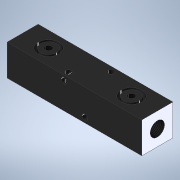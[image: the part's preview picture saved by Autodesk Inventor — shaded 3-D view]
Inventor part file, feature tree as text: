
AUTODESK INVENTOR PART (.ipt)
format: ipt  version: 2021.2 (Build 252289000, 289)  size: 257,024 bytes
history: native  units: in
note: dims shown in document units (in); Inventor stores cm internally (conversion verified against a paired STEP export)
features: sketch x14, hole x11, extrude x3, move_body x2, direct_edit x1
ambient origin geometry x8: Origin, YZ Plane, XZ Plane, XY Plane, X Axis, Y Axis, Z Axis, Center Point
bodies: Solid1 (feature_tree)
feature tree (31):
  extrude  "Extrusion1"  Depth=0.375in
  hole  "Hole3"  [1 undecoded]
  hole  "Hole4"  [1 undecoded]
  hole  "Hole5"  [1 undecoded]
  hole  "Hole6"  [1 undecoded]
  hole  "Hole7"  [1 undecoded]
  extrude  "Extrusion2"  Depth=0.5in
  extrude  "Extrusion3"  Depth=0.5in
  hole  "Hole10"  [1 undecoded]
  hole  "Hole11"  [1 undecoded]
  hole  "Hole12"  [1 undecoded]
  hole  "Hole13"  [1 undecoded]
  direct_edit  "Direct Edit5"
  hole  "Hole14"  [1 undecoded]
  hole  "Hole15"  [1 undecoded]
  sketch  "Sketch1"  dims[d6=0.75in d7=0.0in d34=0.375in]
  sketch  "Sketch4"  dims[d35=0.5in]
  sketch  "Sketch5"  dims[d36=0.156in d37=0.375in d38=0.222in d39=0.25in d40=0.5635in d41=0.375in d42=0.0in d43=0.375in]
  sketch  "Sketch6"  dims[d44=0.156in d45=0.375in d46=0.222in d47=0.25in d48=0.5635in d49=0.375in d50=0.0in d51=1.25in]
  sketch  "Sketch7"  dims[d52=0.116in]
  sketch  "Sketch8"  dims[d53=0.144in d54=0.375in d55=0.119in d56=0.25in d57=0.5635in d58=0.375in d59=0.0in d60=1.25in]
  sketch  "Sketch9"  dims[d61=0.116in]
  sketch  "Sketch11"  dims[d62=0.144in d63=0.375in d64=0.119in d65=0.25in d66=0.5635in d67=0.375in d68=0.0in d69=0.116in]
  sketch  "Sketch13"  dims[d70=1.25in d71=1.25in]
  sketch  "Sketch14"  dims[d72=0.116in]
  sketch  "Sketch15"  dims[d73=0.144in d74=0.375in d75=0.119in d76=0.25in d77=0.5635in d78=0.375in d79=0.0in d82=0.5in]
  sketch  "Sketch16"  dims[d83=0.38in d84=0.5in]
  sketch  "Sketch17"  dims[d85=0.2in d86=0.0in d97=0.38in]
  sketch  "Sketch18"  dims[d98=0.5in d99=0.2in d100=0.0in d113=0.5in d114=0.155in d115=0.0625in d116=0.75in d117=0.119in d118=0.25in d119=0.5635in d120=0.5625in d121=0.0in d122=0.5in d123=0.155in d124=0.0625in d125=0.75in d126=0.119in d127=0.25in d128=0.5635in d129=0.5625in d130=0.0in d131=0.5in d132=0.155in d133=0.156in d134=0.17in d135=0.119in d136=0.25in d137=0.5635in d138=0.17in d139=0.0in d140=0.5in d141=0.155in d142=0.156in d143=0.17in d144=0.119in d145=0.25in d146=0.5635in d147=0.17in d148=0.0in d161=0.125in d162=0.0in d163=0.0in d164=0.0in d165=0.0in d166=0.125in d167=0.375in d168=0.375in d169=0.313in d170=0.2726in d171=0.0246in d172=0.3269in d173=0.375in d174=0.25in d175=0.5635in d176=2.0in d177=0.0in d178=0.375in d179=0.375in d180=0.313in d181=0.2726in d182=0.0246in d183=0.3269in d184=0.375in d185=0.25in d186=0.5635in d187=2.0in d188=0.0in d23=1.0in d24=1.0in d25=1.0in d26=0.15in d27=0.25in d28=0.375in d29=0.5635in d30=0.75in d31=0.8108in d32=0.0625in d33=0.75in d80=0.375in d87=0.25in d88=0.375in d89=0.5635in d90=0.75in d91=0.8108in d92=0.0625in d93=0.75in d94=0.375in d149=1.0in d150=1.0in d151=1.0in d152=0.15in d153=0.25in d154=0.375in d155=0.5635in d156=0.75in d157=0.8108in d158=0.0625in d159=0.75in d160=0.375in d189=1.0in d190=1.0in d191=1.0in d192=0.15in d193=0.25in d194=0.375in d195=0.5635in d196=0.75in d197=0.8108in d198=0.0625in d199=0.75in d200=0.375in]
  move_body  "Move5"
  move_body  "Move6"
note: 11 required parameter values undecoded (feature->parameter linkage not recoverable at this tier; creation-order binding heuristic only, values carry confidence <= 0.55)
